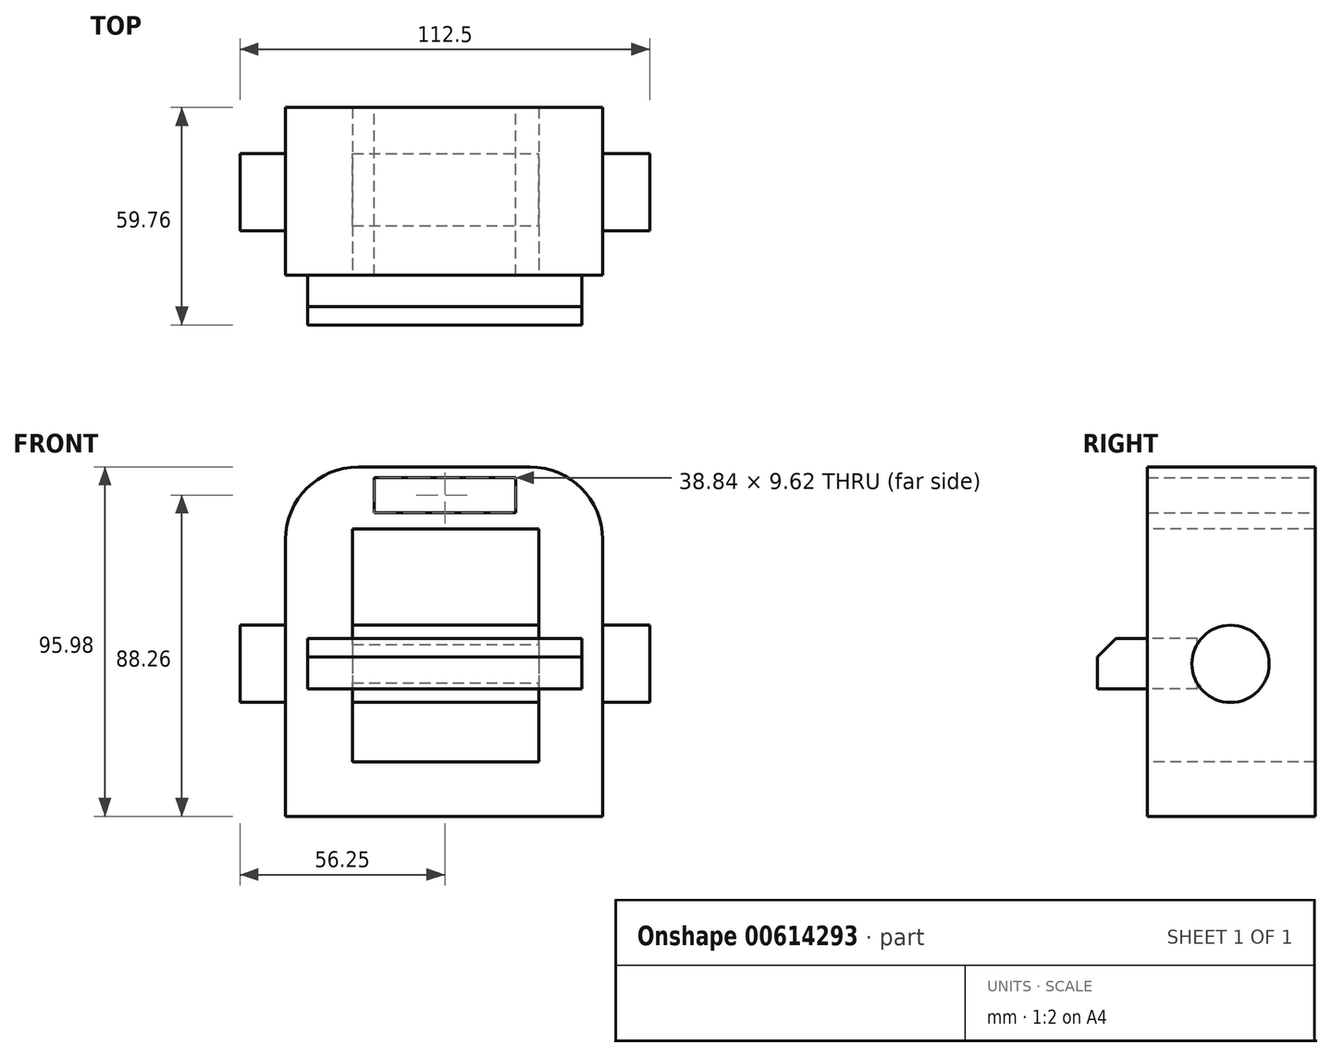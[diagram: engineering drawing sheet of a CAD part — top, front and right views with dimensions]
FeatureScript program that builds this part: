
annotation { "Feature Type Name" : "Feature", "Feature Type Description" : "" }
export const myFeature = defineFeature(function(context is Context, id is Id, definition is map)
    precondition{}
    {
        {
            var Q0;
            Q0=qCreatedBy(makeId("Front.planeOp"),FACE);
            var sketch = newSketch(context, id + "F0", { "sketchPlane" : qUnion([Q0])});
            skLineSegment(sketch, "E0.bottom", {"start": v(-43.75, 54.09) * mm, "end": v(43.38, 54.09) * mm});
            skLineSegment(sketch, "E0.top", {"start": v(-43.75, -41.9) * mm, "end": v(43.38, -41.9) * mm});
            skLineSegment(sketch, "E0.left", {"start": v(-43.75, 54.09) * mm, "end": v(-43.75, -41.9) * mm});
            skLineSegment(sketch, "E0.right", {"start": v(43.38, 54.09) * mm, "end": v(43.38, -41.9) * mm});
            skSolve(sketch);
        }
        {
            var Q0;
            Q0=makeQuery(id+"F0.imprint","IMPRINT",FACE,{"disambiguationData":[TD([[makeQuery(id+"F0.imprint","IMPRINT",EDGE,{"derivedFrom":sQuery(id+"F0.wireOp",EDGE,"E0.bottom")}),-1.0]])]});
            extrude(context, id + "F1", {"entities" : qUnion([Q0]), "depth" : 46.1 * mm, "offsetDistance" : 25.4 * mm});
        }
        {
            var Q0;
            Q0=makeQuery(id+"F1.opExtrude","CAP_FACE",FACE,{"disambiguationData":[OSD([sQuery(id+"F0.wireOp",EDGE,"E0.bottom"),sQuery(id+"F0.wireOp",EDGE,"E0.top"),sQuery(id+"F0.wireOp",EDGE,"E0.left"),sQuery(id+"F0.wireOp",EDGE,"E0.right")])],"isStart":false});
            var sketch = newSketch(context, id + "F2", { "sketchPlane" : qUnion([Q0])});
            skLineSegment(sketch, "E1.bottom", {"start": v(-25.36, 37.1) * mm, "end": v(25.87, 37.1) * mm});
            skLineSegment(sketch, "E1.top", {"start": v(-25.36, -26.9) * mm, "end": v(25.87, -26.9) * mm});
            skLineSegment(sketch, "E1.left", {"start": v(-25.36, 37.1) * mm, "end": v(-25.36, -26.9) * mm});
            skLineSegment(sketch, "E1.right", {"start": v(25.87, 37.1) * mm, "end": v(25.87, -26.9) * mm});
            skSolve(sketch);
        }
        {
            var Q0;
            Q0=makeQuery(id+"F2.imprint","IMPRINT",FACE,{"disambiguationData":[TD([[makeQuery(id+"F2.imprint","IMPRINT",EDGE,{"derivedFrom":sQuery(id+"F2.wireOp",EDGE,"E1.bottom")}),-1.0]])]});
            extrude(context, id + "F3", {"entities" : qUnion([Q0]), "operationType" : NewBodyOperationType.REMOVE, "oppositeDirection" : true, "depth" : 79.97 * mm, "offsetDistance" : 25.4 * mm});
        }
        {
            var Q0;
            Q0=qCreatedBy(makeId("Right.planeOp"),FACE);
            var sketch = newSketch(context, id + "F4", { "sketchPlane" : qUnion([Q0])});
            skCircle(sketch, "E2", {"center": v(-24.17, 0) * mm, "radius": 8.24 * mm});
            skSolve(sketch);
        }
        {
            var Q0;
            Q0=sQuery(id+"F4.wireOp",EDGE,"E2");
            extrude(context, id + "F5", {"bodyType" : ToolBodyType.SURFACE, "surfaceEntities" : qUnion([Q0]), "depth" : 38.7 * mm, "offsetDistance" : 25.4 * mm});
        }
        {
            var Q0;
            Q0=qCreatedBy(makeId("Right.planeOp"),FACE);
            var sketch = newSketch(context, id + "F6", { "sketchPlane" : qUnion([Q0])});
            skCircle(sketch, "E3", {"center": v(-23.25, 0) * mm, "radius": 10.6 * mm});
            skSolve(sketch);
        }
        {
            var Q0;
            Q0 = qSketchRegion(id + "F6", true);
            extrude(context, id + "F7", {"entities" : qUnion([Q0]), "operationType" : NewBodyOperationType.ADD, "endBound" : BoundingType.SYMMETRIC, "oppositeDirection" : true, "depth" : 112.5 * mm, "offsetDistance" : 25.4 * mm});
        }
        {
            var Q0;
            Q0=makeQuery(id+"F1.opExtrude","CAP_FACE",FACE,{"disambiguationData":[OSD([sQuery(id+"F0.wireOp",EDGE,"E0.bottom"),sQuery(id+"F0.wireOp",EDGE,"E0.top"),sQuery(id+"F0.wireOp",EDGE,"E0.left"),sQuery(id+"F0.wireOp",EDGE,"E0.right")])],"isStart":true});
            var sketch = newSketch(context, id + "F8", { "sketchPlane" : qUnion([Q0])});
            skLineSegment(sketch, "E4.bottom", {"start": v(19.42, 51.18) * mm, "end": v(-19.42, 51.18) * mm});
            skLineSegment(sketch, "E4.top", {"start": v(19.42, 41.56) * mm, "end": v(-19.42, 41.56) * mm});
            skLineSegment(sketch, "E4.left", {"start": v(19.42, 51.18) * mm, "end": v(19.42, 41.56) * mm});
            skLineSegment(sketch, "E4.right", {"start": v(-19.42, 51.18) * mm, "end": v(-19.42, 41.56) * mm});
            skPoint(sketch, "E4.middle", {"position": v(0, 46.37) * mm});
            skSolve(sketch);
        }
        {
            var Q0;
            Q0 = qSketchRegion(id + "F8", true);
            extrude(context, id + "F9", {"entities" : qUnion([Q0]), "operationType" : NewBodyOperationType.REMOVE, "oppositeDirection" : true, "depth" : 59.4 * mm, "offsetDistance" : 25.4 * mm});
        }
        {
            var Q0;
            Q0=makeQuery(id+"F1.opExtrude","CAP_FACE",FACE,{"disambiguationData":[OSD([sQuery(id+"F0.wireOp",EDGE,"E0.bottom"),sQuery(id+"F0.wireOp",EDGE,"E0.top"),sQuery(id+"F0.wireOp",EDGE,"E0.left"),sQuery(id+"F0.wireOp",EDGE,"E0.right")])],"isStart":false});
            var sketch = newSketch(context, id + "F10", { "sketchPlane" : qUnion([Q0])});
            skLineSegment(sketch, "E5.bottom", {"start": v(37.65, 6.93) * mm, "end": v(-37.65, 6.93) * mm});
            skLineSegment(sketch, "E5.top", {"start": v(37.65, -6.93) * mm, "end": v(-37.65, -6.93) * mm});
            skLineSegment(sketch, "E5.left", {"start": v(37.65, 6.93) * mm, "end": v(37.65, -6.93) * mm});
            skLineSegment(sketch, "E5.right", {"start": v(-37.65, 6.93) * mm, "end": v(-37.65, -6.93) * mm});
            skPoint(sketch, "E5.middle", {"position": v(0, 0) * mm});
            skSolve(sketch);
        }
        {
            var Q0;
            Q0 = qSketchRegion(id + "FelAMnok4EyLKcN_2", true);
            var Q1;
            {var subQ0=sQuery(id+"F10.wireOp",EDGE,"E5.bottom");var subQ1=makeQuery(id+"F3.boolean.opBoolean","COPY",EDGE,{"derivedFrom":makeQuery(id+"F3.opExtrude","CAP_EDGE",EDGE,{"disambiguationData":[OSD([sQuery(id+"F2.wireOp",EDGE,"E1.right")])],"isStart":true})});var subQ2=makeQuery(id+"F10.imprint","INTERSECT",VERTEX,{"derivedFrom":[subQ1,subQ0]});Q1=makeQuery(id+"F10.imprint","IMPRINT",FACE,{"disambiguationData":[TD([[makeQuery(id+"F10.imprint","IMPRINT",EDGE,{"disambiguationData":[TD([[subQ2,-1.0]])],"derivedFrom":subQ0}),1.0]])]});}
            var Q2;
            {var subQ0=sQuery(id+"F10.wireOp",EDGE,"E5.left");Q2=makeQuery(id+"F10.imprint","IMPRINT",FACE,{"disambiguationData":[TD([[makeQuery(id+"F10.imprint","IMPRINT",EDGE,{"derivedFrom":subQ0}),-1.0]])]});}
            var Q3;
            {var subQ0=sQuery(id+"F10.wireOp",EDGE,"E5.right");Q3=makeQuery(id+"F10.imprint","IMPRINT",FACE,{"disambiguationData":[TD([[makeQuery(id+"F10.imprint","IMPRINT",EDGE,{"derivedFrom":subQ0}),1.0]])]});}
            extrude(context, id + "F11", {"entities" : qUnion([Q0, Q1, Q2, Q3]), "operationType" : NewBodyOperationType.ADD, "endBound" : BoundingType.SYMMETRIC, "depth" : 27.32 * mm, "offsetDistance" : 25.4 * mm});
        }
        {
            var Q0;
            Q0=makeQuery(id+"F1.opExtrude","SWEPT_EDGE",EDGE,{"disambiguationData":[OSD([sQuery(id+"F0.wireOp",EDGE,"E0.bottom"),sQuery(id+"F0.wireOp",EDGE,"E0.left")])]});
            var Q1;
            Q1=makeQuery(id+"F1.opExtrude","SWEPT_EDGE",EDGE,{"disambiguationData":[OSD([sQuery(id+"F0.wireOp",EDGE,"E0.bottom"),sQuery(id+"F0.wireOp",EDGE,"E0.right")])]});
            fillet(context, id + "F12", {"entities" : qUnion([Q0, Q1]), "radius" : 20 * mm, "tangentPropagation" : true, "allowEdgeOverflow" : false});
        }
        {
            var Q0;
            Q0=makeQuery(id+"F11.opExtrude","CAP_EDGE",EDGE,{"disambiguationData":[OSD([sQuery(id+"F10.wireOp",EDGE,"E5.bottom")])],"isStart":false});
            chamfer(context, id + "F13", {"entities" : qUnion([Q0]), "width" : 5.08 * mm, "tangentPropagation" : true});
        }
    });
